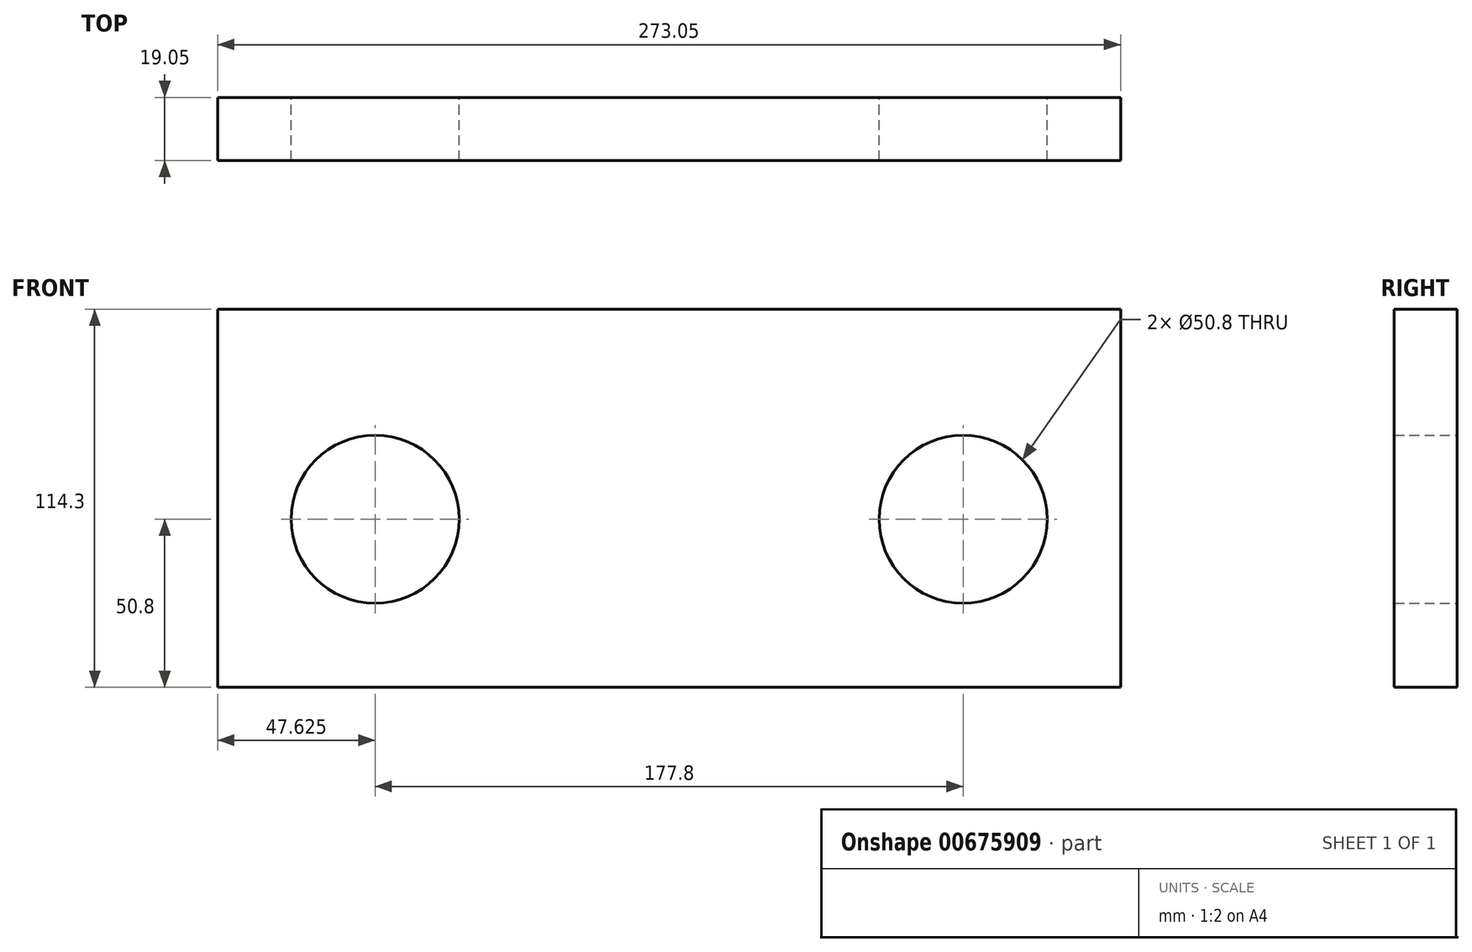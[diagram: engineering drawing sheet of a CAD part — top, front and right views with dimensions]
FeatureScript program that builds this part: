
annotation { "Feature Type Name" : "Feature", "Feature Type Description" : "" }
export const myFeature = defineFeature(function(context is Context, id is Id, definition is map)
    precondition{}
    {
        {
            var Q0;
            Q0=qCreatedBy(makeId("Front.planeOp"),FACE);
            var sketch = newSketch(context, id + "F0", { "sketchPlane" : qUnion([Q0])});
            skLineSegment(sketch, "E0.bottom", {"start": v(0, 0) * mm, "end": v(273.05, 0) * mm});
            skLineSegment(sketch, "E0.top", {"start": v(0, 114.3) * mm, "end": v(273.05, 114.3) * mm});
            skLineSegment(sketch, "E0.left", {"start": v(0, 0) * mm, "end": v(0, 114.3) * mm});
            skLineSegment(sketch, "E0.right", {"start": v(273.05, 0) * mm, "end": v(273.05, 114.3) * mm});
            skSolve(sketch);
        }
        {
            var Q0;
            Q0=makeQuery(id+"F0.imprint","IMPRINT",FACE,{"disambiguationData":[TD([[makeQuery(id+"F0.imprint","IMPRINT",EDGE,{"derivedFrom":sQuery(id+"F0.wireOp",EDGE,"E0.bottom")}),1.0]])]});
            var sketch = newSketch(context, id + "F1", { "sketchPlane" : qUnion([Q0])});
            skCircle(sketch, "E1", {"center": v(47.63, 50.8) * mm, "radius": 25.4 * mm});
            skCircle(sketch, "E2", {"center": v(225.43, 50.8) * mm, "radius": 25.4 * mm});
            skSolve(sketch);
        }
        {
            var Q0;
            Q0=makeQuery(id+"F1.imprint","IMPRINT",FACE,{"disambiguationData":[TD([[makeQuery(id+"F1.imprint","IMPRINT",EDGE,{"derivedFrom":sQuery(id+"F1.wireOp",EDGE,"E1")}),-1.0]])]});
            extrude(context, id + "F2", {"entities" : qUnion([Q0]), "depth" : 19.05 * mm, "offsetDistance" : 25.4 * mm});
        }
        {
            var Q0;
            Q0 = qSketchRegion(id + "F1", true);
            extrude(context, id + "F3", {"entities" : qUnion([Q0]), "operationType" : NewBodyOperationType.REMOVE, "oppositeDirection" : true, "depth" : 25.4 * mm, "offsetDistance" : 25.4 * mm});
        }
    });
